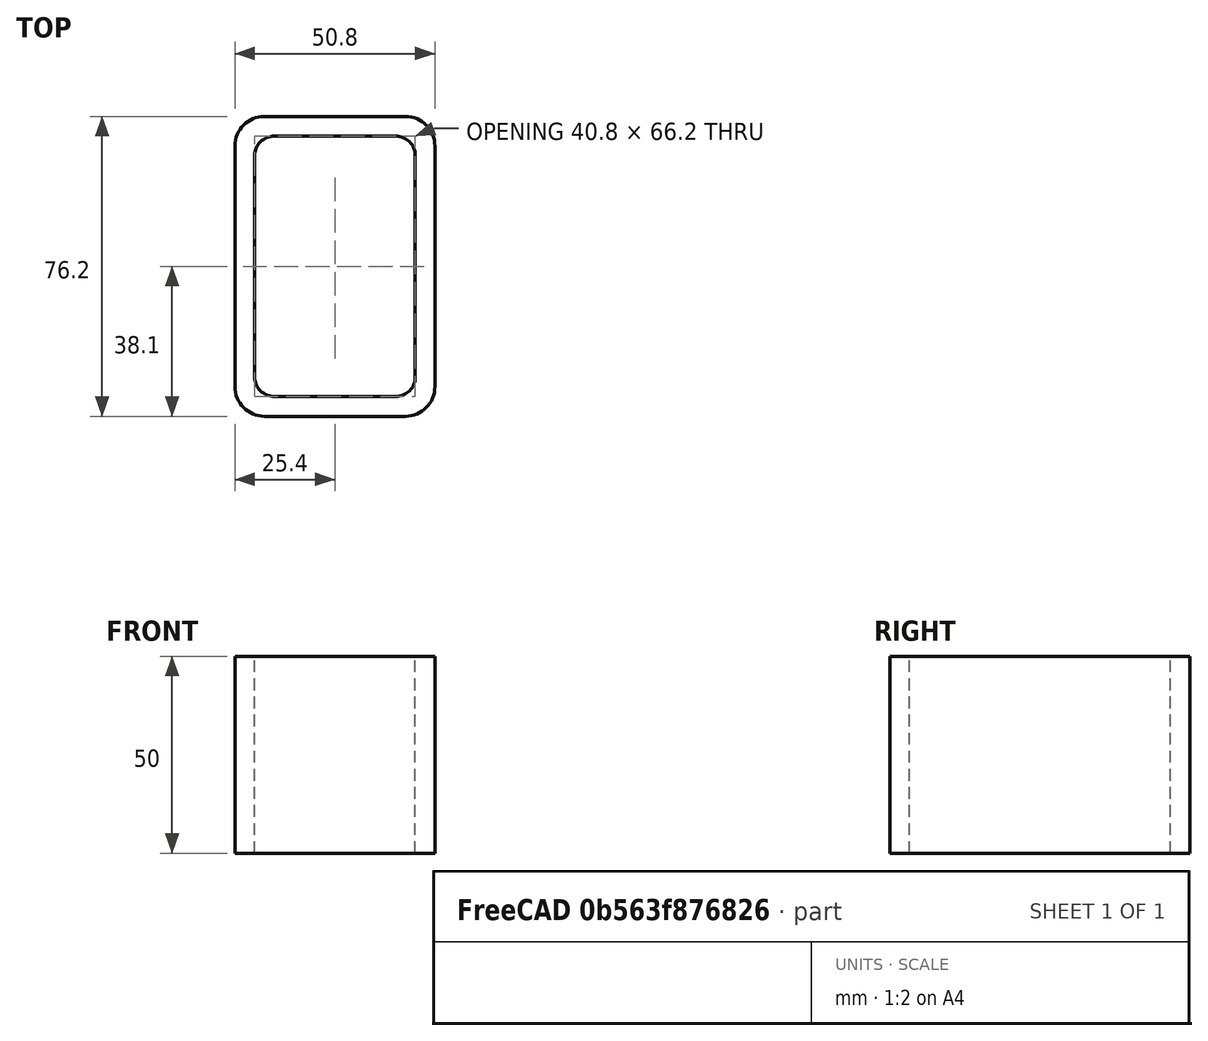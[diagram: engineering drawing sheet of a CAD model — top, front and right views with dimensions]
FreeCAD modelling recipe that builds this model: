
FCSTD DOCUMENT  (FreeCAD 0.15R4671 (Git))
Label: Rectangular hollow section 76.2 x50.8 x5 EN10219 S235JRH
License: All rights reserved
LicenseURL: http://en.wikipedia.org/wiki/All_rights_reserved
objects: Sketcher::SketchObject×1, Part::Extrusion×1
note: 2 computed .brp shape members not serialized (recipe doc carries the construction recipe); baked Part::Feature solids carry a one-line shape summary decoded from their .brp

FEATURE [Sketcher::SketchObject] Sketch
  sketch-geometry (16):
    g0: LineSegment StartX=-15.4 StartY=33.1 StartZ=0 EndX=15.4 EndY=33.1 EndZ=0
    g1: LineSegment StartX=20.4 StartY=28.1 StartZ=0 EndX=20.4 EndY=-28.1 EndZ=0
    g2: LineSegment StartX=15.4 StartY=-33.1 StartZ=0 EndX=-15.4 EndY=-33.1 EndZ=0
    g3: LineSegment StartX=-20.4 StartY=-28.1 StartZ=0 EndX=-20.4 EndY=28.1 EndZ=0
    g4: LineSegment StartX=-17.9 StartY=38.1 StartZ=0 EndX=17.9 EndY=38.1 EndZ=0
    g5: LineSegment StartX=25.4 StartY=30.6 StartZ=0 EndX=25.4 EndY=-30.6 EndZ=0
    g6: LineSegment StartX=17.9 StartY=-38.1 StartZ=0 EndX=-17.9 EndY=-38.1 EndZ=0
    g7: LineSegment StartX=-25.4 StartY=-30.6 StartZ=0 EndX=-25.4 EndY=30.6 EndZ=0
    g8: ArcOfCircle CenterX=-15.4 CenterY=28.1 CenterZ=0 NormalX=0 NormalY=0 NormalZ=1 Radius=5 StartAngle=1.5708 EndAngle=3.14159
    g9: ArcOfCircle CenterX=15.4 CenterY=28.1 CenterZ=0 NormalX=0 NormalY=0 NormalZ=1 Radius=5 StartAngle=0 EndAngle=1.5708
    g10: ArcOfCircle CenterX=15.4 CenterY=-28.1 CenterZ=0 NormalX=0 NormalY=0 NormalZ=1 Radius=5 StartAngle=4.71239 EndAngle=6.28319
    g11: ArcOfCircle CenterX=-15.4 CenterY=-28.1 CenterZ=0 NormalX=0 NormalY=0 NormalZ=1 Radius=5 StartAngle=3.14159 EndAngle=4.71239
    g12: ArcOfCircle CenterX=17.9 CenterY=30.6 CenterZ=0 NormalX=0 NormalY=0 NormalZ=1 Radius=7.5 StartAngle=0 EndAngle=1.5708
    g13: ArcOfCircle CenterX=17.9 CenterY=-30.6 CenterZ=0 NormalX=0 NormalY=0 NormalZ=1 Radius=7.5 StartAngle=4.71239 EndAngle=6.28319
    g14: ArcOfCircle CenterX=-17.9 CenterY=-30.6 CenterZ=0 NormalX=0 NormalY=0 NormalZ=1 Radius=7.5 StartAngle=3.14159 EndAngle=4.71239
    g15: ArcOfCircle CenterX=-17.9 CenterY=30.6 CenterZ=0 NormalX=0 NormalY=0 NormalZ=1 Radius=7.5 StartAngle=1.5708 EndAngle=3.14159
  constraints (36):
    c: Horizontal(g2)
    c: Vertical(g3)
    c: Horizontal(g6)
    c: Vertical(g7)
    c: Tangent(g3,g8) = 1.5708
    c: Tangent(g0,g8) = 1.5708
    c: Tangent(g0,g9) = 1.5708
    c: Tangent(g1,g9) = 1.5708
    c: Tangent(g1,g10) = 1.5708
    c: Tangent(g2,g10) = 1.5708
    c: Tangent(g2,g11) = 1.5708
    c: Tangent(g3,g11) = 1.5708
    c: Tangent(g4,g12) = 1.5708
    c: Tangent(g5,g12) = 1.5708
    c: Tangent(g5,g13) = 1.5708
    c: Tangent(g6,g13) = 1.5708
    c: Tangent(g6,g14) = 1.5708
    c: Tangent(g7,g14) = 1.5708
    c: Tangent(g7,g15) = 1.5708
    c: Tangent(g4,g15) = 1.5708
    c: Equal(g9,g8)
    c: Equal(g9,g11)
    c: Equal(g9,g10)
    c: Equal(g12,g15)
    c: Equal(g12,g14)
    c: Equal(g12,g13)
    c: Symmetric(g4,g6,g-1)
    c: Symmetric(g7,g5,g-2)
    c: DistanceY(g4,g6) = -76.2
    c: DistanceX(g7,g5) = 50.8
    c: Symmetric(g3,g1,g-2)
    c: Symmetric(g0,g2,g-1)
    c: DistanceY(g0,g4) = 5
    c: DistanceX(g5,g1) = -5
    c: Radius(g9) = 5
    c: Radius(g12) = 7.5
FEATURE [Part::Extrusion] Extrude  label="Rectangular hollow section 76.2 x50.8 x5 EN10219 S235JRH"
  Base = -> Sketch
  Dir = (0,0,50)
  Solid = true
